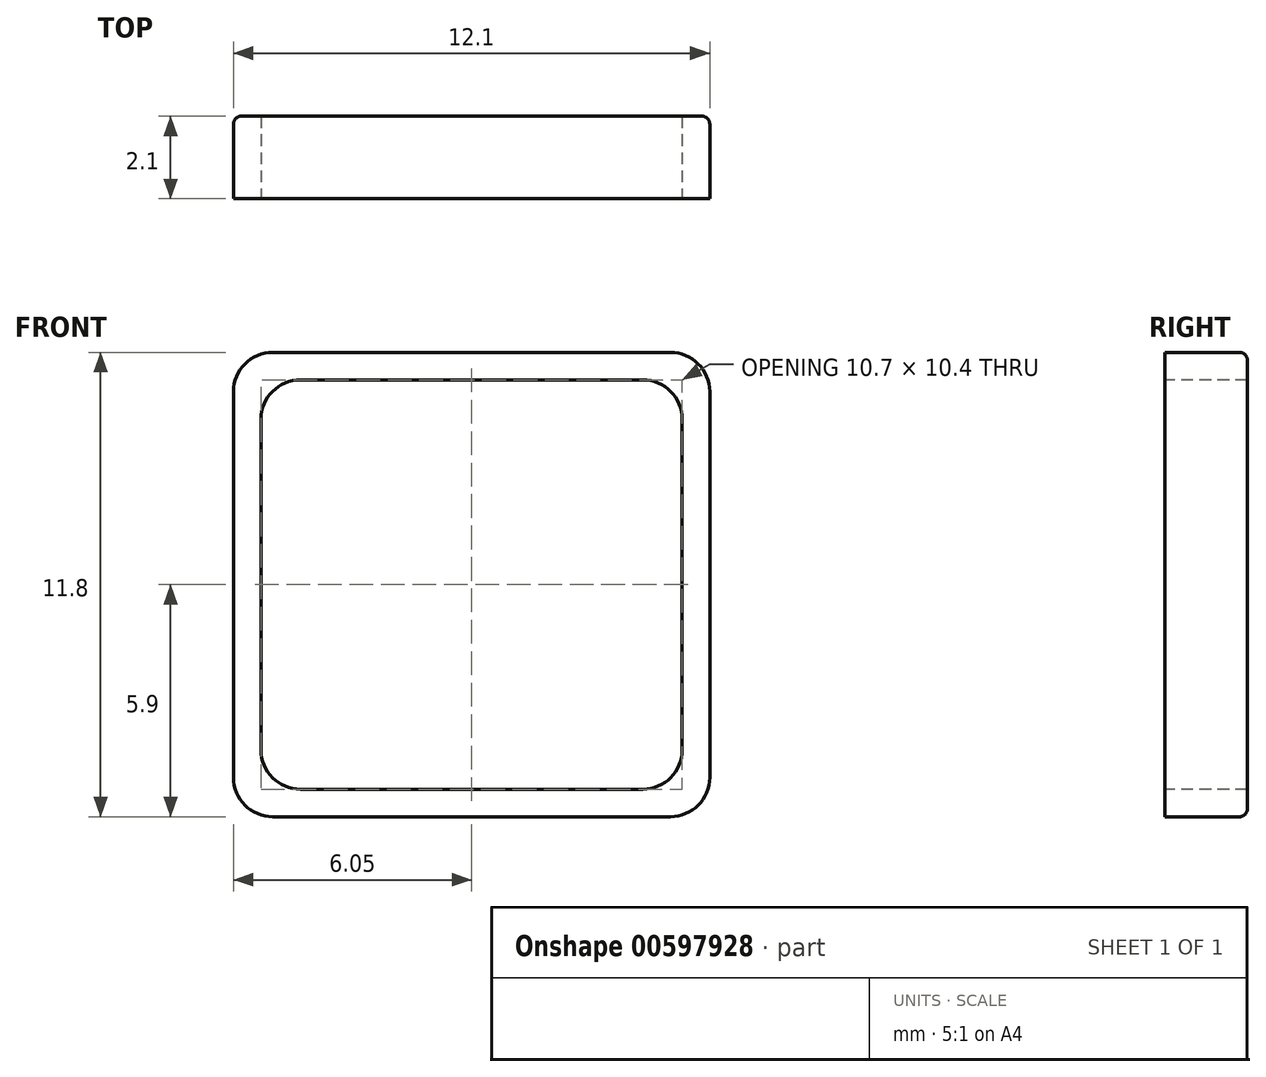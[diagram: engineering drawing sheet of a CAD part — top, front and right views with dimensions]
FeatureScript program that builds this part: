
annotation { "Feature Type Name" : "Feature", "Feature Type Description" : "" }
export const myFeature = defineFeature(function(context is Context, id is Id, definition is map)
    precondition{}
    {
        {
            var Q0;
            Q0=qCreatedBy(makeId("Front.planeOp"),FACE);
            var sketch = newSketch(context, id + "F0", { "sketchPlane" : qUnion([Q0])});
            skLineSegment(sketch, "E0.bottom", {"start": v(-28.8, 119.9) * mm, "end": v(-38.9, 119.9) * mm});
            skLineSegment(sketch, "E0.top", {"start": v(-28.8, 108.1) * mm, "end": v(-38.9, 108.1) * mm});
            skLineSegment(sketch, "E0.left", {"start": v(-27.8, 118.9) * mm, "end": v(-27.8, 109.1) * mm});
            skLineSegment(sketch, "E0.right", {"start": v(-39.9, 118.9) * mm, "end": v(-39.9, 109.1) * mm});
            skLineSegment(sketch, "E1.bottom", {"start": v(-29.5, 119.2) * mm, "end": v(-38.2, 119.2) * mm});
            skLineSegment(sketch, "E1.top", {"start": v(-29.5, 108.8) * mm, "end": v(-38.2, 108.8) * mm});
            skLineSegment(sketch, "E1.left", {"start": v(-28.5, 118.2) * mm, "end": v(-28.5, 109.8) * mm});
            skLineSegment(sketch, "E1.right", {"start": v(-39.2, 118.2) * mm, "end": v(-39.2, 109.8) * mm});
            skPoint(sketch, "E2.visualSharp", {"position": v(-28.5, 119.2) * mm});
            skArc(sketch, "E2.filletArc", {"start": v(-28.5, 118.2) * mm, "mid": v(-28.8, 118.9) * mm, "end": v(-29.5, 119.2) * mm});
            skPoint(sketch, "E3.visualSharp", {"position": v(-39.2, 119.2) * mm});
            skArc(sketch, "E3.filletArc", {"start": v(-38.2, 119.2) * mm, "mid": v(-38.9, 118.9) * mm, "end": v(-39.2, 118.2) * mm});
            skPoint(sketch, "E4.visualSharp", {"position": v(-39.2, 108.8) * mm});
            skArc(sketch, "E4.filletArc", {"start": v(-39.2, 109.8) * mm, "mid": v(-38.9, 109.1) * mm, "end": v(-38.2, 108.8) * mm});
            skPoint(sketch, "E5.visualSharp", {"position": v(-28.5, 108.8) * mm});
            skArc(sketch, "E5.filletArc", {"start": v(-29.5, 108.8) * mm, "mid": v(-28.8, 109.1) * mm, "end": v(-28.5, 109.8) * mm});
            skPoint(sketch, "E6.visualSharp", {"position": v(-27.8, 108.1) * mm});
            skArc(sketch, "E6.filletArc", {"start": v(-28.8, 108.1) * mm, "mid": v(-28.1, 108.4) * mm, "end": v(-27.8, 109.1) * mm});
            skPoint(sketch, "E7.visualSharp", {"position": v(-39.9, 108.1) * mm});
            skArc(sketch, "E7.filletArc", {"start": v(-39.9, 109.1) * mm, "mid": v(-39.6, 108.4) * mm, "end": v(-38.9, 108.1) * mm});
            skPoint(sketch, "E8.visualSharp", {"position": v(-39.9, 119.9) * mm});
            skArc(sketch, "E8.filletArc", {"start": v(-38.9, 119.9) * mm, "mid": v(-39.6, 119.6) * mm, "end": v(-39.9, 118.9) * mm});
            skPoint(sketch, "E9.visualSharp", {"position": v(-27.8, 119.9) * mm});
            skArc(sketch, "E9.filletArc", {"start": v(-27.8, 118.9) * mm, "mid": v(-28.1, 119.6) * mm, "end": v(-28.8, 119.9) * mm});
            skSolve(sketch);
        }
        {
            var Q0;
            Q0 = qSketchRegion(id + "F0", true);
            extrude(context, id + "F1", {"entities" : qUnion([Q0]), "oppositeDirection" : true, "depth" : 2.1 * mm, "offsetDistance" : 25 * mm});
        }
        {
            var Q0;
            Q0=makeQuery(id+"F1.opExtrude","CAP_EDGE",EDGE,{"disambiguationData":[OSD([sQuery(id+"F0.wireOp",EDGE,"E0.right")])],"isStart":false});
            var Q1;
            Q1=makeQuery(id+"F1.opExtrude","CAP_EDGE",EDGE,{"disambiguationData":[OSD([sQuery(id+"F0.wireOp",EDGE,"E0.bottom")])],"isStart":false});
            var Q2;
            Q2=makeQuery(id+"F1.opExtrude","CAP_EDGE",EDGE,{"disambiguationData":[OSD([sQuery(id+"F0.wireOp",EDGE,"E0.top")])],"isStart":false});
            var Q3;
            Q3=makeQuery(id+"F1.opExtrude","CAP_EDGE",EDGE,{"disambiguationData":[OSD([sQuery(id+"F0.wireOp",EDGE,"E6.filletArc")])],"isStart":false});
            var Q4;
            Q4=makeQuery(id+"F1.opExtrude","CAP_EDGE",EDGE,{"disambiguationData":[OSD([sQuery(id+"F0.wireOp",EDGE,"E9.filletArc")])],"isStart":false});
            var Q5;
            Q5=makeQuery(id+"F1.opExtrude","CAP_EDGE",EDGE,{"disambiguationData":[OSD([sQuery(id+"F0.wireOp",EDGE,"E8.filletArc")])],"isStart":false});
            var Q6;
            Q6=makeQuery(id+"F1.opExtrude","CAP_EDGE",EDGE,{"disambiguationData":[OSD([sQuery(id+"F0.wireOp",EDGE,"E7.filletArc")])],"isStart":false});
            var Q7;
            Q7=makeQuery(id+"F1.opExtrude","CAP_EDGE",EDGE,{"disambiguationData":[OSD([sQuery(id+"F0.wireOp",EDGE,"E0.left")])],"isStart":false});
            fillet(context, id + "F2", {"entities" : qUnion([Q0, Q1, Q2, Q3, Q4, Q5, Q6, Q7]), "radius" : 0.2 * mm, "tangentPropagation" : true, "allowEdgeOverflow" : false});
        }
    });
